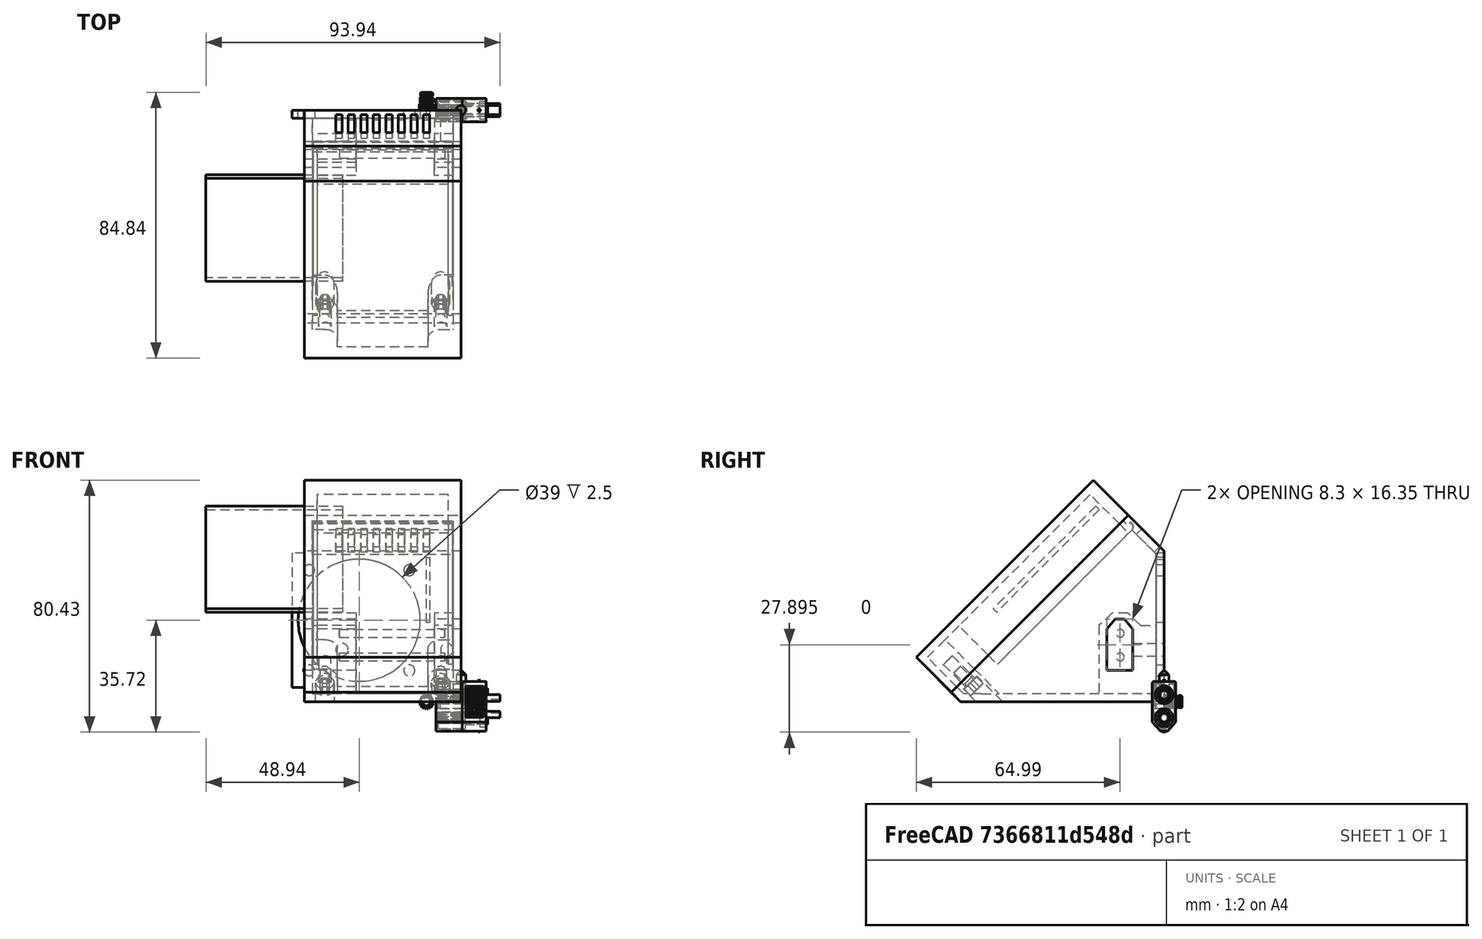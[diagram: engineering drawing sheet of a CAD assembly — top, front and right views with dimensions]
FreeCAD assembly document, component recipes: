
FREECAD ASSEMBLY — COMPONENT RECIPES ("moduleUSB_SimpleDual_001_SurBase35mm_012")

This assembly document has 12 components, labeled P0..P11 below (a component is one placed body or linked part). 5 of them carry a construction recipe — the FreeCAD feature program that regenerates the part from scratch, quoted from this document or its linked companion documents; the rest are supplied as boundary geometry only. No exploded tour is included for this assembly.
COMPONENT P0 — recipe-attached ("base", modeled in this document).
Construction recipe (the document's own serialized feature program — sketch geometry with constraints, then the solid features built on it; lengths are millimeters unless a unit is written):

FEATURE [PartDesign::FeatureBase] Clone
  BaseFeature = -> Slice_child0
FEATURE [PartDesign::Thickness] Thickness
  Base = -> Clone [Face7]
  BaseFeature = -> Clone
  Intersection = false
  Join = 0
  Mode = 0
  Reversed = true
  SupportTransform = false
  Value = 2.5
  expr: Value = <<sp>>.epaisseurParois
FEATURE [PartDesign::Plane] DatumPlane001  label="planXt"
  AttachmentOffset = pos=(0,0,-2.5) rot=(0,0,1;0rad)
  Length = 110.737
  MapMode = 5
  Placement = pos=(-2.5,6e-16,-6e-16) rot=(0.57735,0.57735,0.57735;2.0944rad)
  ResizeMode = 0
  Support = -> [YZ_Plane002]
  Width = 102.305
  expr: .AttachmentOffset.Base.z = -<<sp>>.epaisseurParois
FEATURE [Sketcher::SketchObject] Sketch002  label="sk_renfortXt"
  FullyConstrained = true
  MapMode = 5
  Placement = pos=(-2.5,6e-16,-6e-16) rot=(0.57735,0.57735,0.57735;2.0944rad)
  Support = -> [DatumPlane001]
  expr: .Constraints.dist = <<sp>>.xt60distanceAngleBord
  expr: .Constraints.epRf = <<sp>>.xt60epRenfort
  expr: Constraints[13] = <<sp>>.xt60largeurFetiere
  expr: Constraints[14] = <<sp>>.xt60hauteur
  expr: Constraints[15] = <<sp>>.xt60hauteurToit
  expr: Constraints[16] = <<sp>>.xt60base
  expr: Constraints[18] = .Constraints.dist
  expr: Constraints[31] = <<sp>>.epaisseurParois
  expr: Constraints[32] = .Constraints.epRf
  expr: Constraints[34] = .Constraints.epRf
  expr: Constraints[45] = <<sp>>.epaisseurParois
  sketch-geometry (17):
    g0: LineSegment StartX=-18.3 StartY=10 StartZ=0 EndX=-18.3 EndY=23.25 EndZ=0
    g1: LineSegment StartX=-18.3 StartY=23.25 StartZ=0 EndX=-15.65 EndY=25.75 EndZ=0
    g2: LineSegment StartX=-15.65 StartY=25.75 StartZ=0 EndX=-12.65 EndY=25.75 EndZ=0
    g3: LineSegment StartX=-12.65 StartY=25.75 StartZ=0 EndX=-10 EndY=23.25 EndZ=0
    g4: LineSegment StartX=-10 StartY=23.25 StartZ=0 EndX=-10 EndY=10 EndZ=0
    g5: LineSegment StartX=-10 StartY=10 StartZ=0 EndX=-18.3 EndY=10 EndZ=0
    g6: LineSegment StartX=-14.15 StartY=10 StartZ=0 EndX=-14.15 EndY=25.75 EndZ=0
    g7: LineSegment StartX=-16.6431 StartY=28.25 StartZ=0 EndX=-20.8 EndY=24.3284 EndZ=0
    g8: LineSegment StartX=-20.8 StartY=24.3284 StartZ=0 EndX=-20.8 EndY=2.5 EndZ=0
    g9: LineSegment StartX=-20.8 StartY=2.5 StartZ=0 EndX=-7.5 EndY=2.5 EndZ=0
    g10: LineSegment StartX=-7.5 StartY=2.5 StartZ=0 EndX=-7.5 EndY=24.3284 EndZ=0
    g11: LineSegment StartX=-7.5 StartY=24.3284 StartZ=0 EndX=-11.6569 EndY=28.25 EndZ=0
    g12: LineSegment StartX=-11.6569 StartY=28.25 StartZ=0 EndX=-16.6431 EndY=28.25 EndZ=0
    g13: LineSegment StartX=-7.5 StartY=24.3284 StartZ=0 EndX=-2.5 EndY=24.3284 EndZ=0
    g14: LineSegment StartX=-2.5 StartY=24.3284 StartZ=0 EndX=-2.5 EndY=2.5 EndZ=0
    g15: LineSegment StartX=-2.5 StartY=2.5 StartZ=0 EndX=-7.5 EndY=2.5 EndZ=0
    g16: LineSegment StartX=-7.5 StartY=2.5 StartZ=0 EndX=-7.5 EndY=24.3284 EndZ=0
  constraints (46):
    c: Vertical(g0)
    c: Coincident(g0,g1)
    c: Coincident(g1,g2)
    c: Horizontal(g2)
    c: Coincident(g2,g3)
    c: Coincident(g3,g4)
    c: Vertical(g4)
    c: Coincident(g4,g5)
    c: Coincident(g5,g0)
    c: Horizontal(g5)
    c: Symmetric(g1,g2,g6)
    c: Equal(g0,g4)
    c: Symmetric(g0,g4,g6)
    c: DistanceX(g2,g2) = 3
    c: DistanceY(g4,g4) = 13.25
    c: DistanceY(g3,g2) = 2.5
    c: DistanceX(g5,g5) = 8.3
    c: DistanceX(g4,g-1) = 10  'dist'
    c: DistanceY(g-1,g4) = 10
    c: Coincident(g7,g8)
    c: Vertical(g8)
    c: Coincident(g8,g9)
    c: Horizontal(g9)
    c: Coincident(g9,g10)
    c: Coincident(g10,g11)
    c: Coincident(g11,g12)
    c: Coincident(g12,g7)
    c: Symmetric(g7,g10,g6)
    c: Symmetric(g7,g11,g6)
    c: Symmetric(g8,g9,g6)
    c: DistanceX(g8,g0) = 2.5  'epRf'
    c: DistanceY(g-1,g9) = 2.5
    c: Distance(g7,g1) = 2.5
    c: Parallel(g1,g7)
    c: DistanceY(g2,g11) = 2.5
    c: Coincident(g13,g14)
    c: Coincident(g14,g15)
    c: Coincident(g15,g16)
    c: Coincident(g16,g13)
    c: Horizontal(g13)
    c: Horizontal(g15)
    c: Vertical(g14)
    c: Vertical(g16)
    c: Coincident(g13,g11)
    c: Horizontal(g14,g9)
    c: DistanceX(g14,g-1) = 2.5
FEATURE [PartDesign::Pad] Pad001  label="renfortXt"
  AllowMultiFace = false
  BaseFeature = -> Thickness
  Direction = (1,-1e-16,1e-16)
  Length = 45
  Length2 = 100
  Profile = -> Sketch002
  Reversed = true
  Type = 0
  expr: Length = <<sp>>.largeurModuleBase - 2 * <<sp>>.epaisseurParois
FEATURE [Sketcher::SketchObject] Sketch003  label="sk_trouXt"
  FullyConstrained = true
  MapMode = 5
  Placement = pos=(0,0,0) rot=(0.57735,0.57735,0.57735;2.0944rad)
  Support = -> [YZ_Plane002]
  expr: .Constraints.dist = <<sp>>.xt60distanceAngleBord
  expr: Constraints[13] = <<sp>>.xt60base
  expr: Constraints[14] = <<sp>>.xt60hauteur
  expr: Constraints[15] = <<sp>>.xt60hauteurToit + <<sp>>.xtJeu
  expr: Constraints[16] = <<sp>>.xt60largeurFetiere
  expr: Constraints[18] = .Constraints.dist
  sketch-geometry (7):
    g0: LineSegment StartX=-18.3 StartY=10 StartZ=0 EndX=-18.3 EndY=23.25 EndZ=0
    g1: LineSegment StartX=-18.3 StartY=23.25 StartZ=0 EndX=-15.65 EndY=26.35 EndZ=0
    g2: LineSegment StartX=-15.65 StartY=26.35 StartZ=0 EndX=-12.65 EndY=26.35 EndZ=0
    g3: LineSegment StartX=-12.65 StartY=26.35 StartZ=0 EndX=-10 EndY=23.25 EndZ=0
    g4: LineSegment StartX=-10 StartY=23.25 StartZ=0 EndX=-10 EndY=10 EndZ=0
    g5: LineSegment StartX=-10 StartY=10 StartZ=0 EndX=-18.3 EndY=10 EndZ=0
    g6: LineSegment StartX=-14.15 StartY=10 StartZ=0 EndX=-14.15 EndY=26.35 EndZ=0
  constraints (19):
    c: Vertical(g0)
    c: Coincident(g0,g1)
    c: Coincident(g1,g2)
    c: Horizontal(g2)
    c: Coincident(g2,g3)
    c: Coincident(g3,g4)
    c: Coincident(g4,g5)
    c: Coincident(g5,g0)
    c: Horizontal(g5)
    c: Symmetric(g1,g2,g6)
    c: Symmetric(g0,g3,g6)
    c: Vertical(g6)
    c: Symmetric(g0,g4,g6)
    c: DistanceX(g5,g5) = 8.3
    c: DistanceY(g4,g4) = 13.25
    c: DistanceY(g3,g2) = 3.1
    c: DistanceX(g2,g2) = 3
    c: DistanceX(g4,g-1) = 10  'dist'
    c: DistanceY(g-1,g4) = 10
FEATURE [PartDesign::Pocket] Pocket
  AllowMultiFace = false
  BaseFeature = -> Pad001
  Direction = (-1,2e-16,-3e-16)
  Length = 50
  Length2 = 100
  Profile = -> Sketch003
  Type = 0
  expr: Length = <<sp>>.largeurModuleBase
FEATURE [PartDesign::Plane] DatumPlane002  label="planDecoupeRenfortXt"
  AttachmentOffset = pos=(0,0,2.5) rot=(0,0,1;0rad)
  Length = 99.1505
  MapMode = 5
  Placement = pos=(0,-2.5,-6e-16) rot=(1,0,0;1.5708rad)
  ResizeMode = 0
  Support = -> [XZ_Plane002]
  Width = 101.269
  expr: .AttachmentOffset.Base.z = <<sp>>.epaisseurParois
FEATURE [Sketcher::SketchObject] Sketch004  label="sk_decoupRenfXt"
  FullyConstrained = true
  MapMode = 5
  Placement = pos=(0,-2.5,-6e-16) rot=(1,0,0;1.5708rad)
  Support = -> [DatumPlane002]
  expr: Constraints[10] = <<sp>>.xt60LongueurRenfortPetit + <<sp>>.epaisseurParois
  expr: Constraints[11] = <<sp>>.largeurModuleBase - (<<sp>>.xt60longueurRenfortGrand + <<sp>>.epaisseurParois)
  expr: Constraints[8] = <<sp>>.epaisseurParois
  expr: Constraints[9] = <<sp>>.xt60distanceAngleBord + <<sp>>.xt60hauteur + <<sp>>.xt60hauteurToit + <<sp>>.xt60epRenfort
  sketch-geometry (4):
    g0: LineSegment StartX=-33.5 StartY=28.25 StartZ=0 EndX=-8.5 EndY=28.25 EndZ=0
    g1: LineSegment StartX=-8.5 StartY=28.25 StartZ=0 EndX=-8.5 EndY=2.5 EndZ=0
    g2: LineSegment StartX=-8.5 StartY=2.5 StartZ=0 EndX=-33.5 EndY=2.5 EndZ=0
    g3: LineSegment StartX=-33.5 StartY=2.5 StartZ=0 EndX=-33.5 EndY=28.25 EndZ=0
  constraints (12):
    c: Coincident(g0,g1)
    c: Coincident(g1,g2)
    c: Coincident(g2,g3)
    c: Coincident(g3,g0)
    c: Horizontal(g0)
    c: Horizontal(g2)
    c: Vertical(g1)
    c: Vertical(g3)
    c: DistanceY(g-1,g1) = 2.5
    c: DistanceY(g-1,g0) = 28.25
    c: DistanceX(g1,g-1) = 8.5
    c: DistanceX(g2,g-1) = 33.5
FEATURE [PartDesign::Pocket] Pocket001  label="decoupeRenfXt"
  AllowMultiFace = false
  BaseFeature = -> Pocket
  Direction = (0,1,2e-16)
  Length = 23.3
  Length2 = 100
  Profile = -> Sketch004
  Reversed = true
  Type = 0
  expr: Length = <<sp>>.xt60distanceAngleBord + <<sp>>.xt60base + 2 * <<sp>>.xt60epRenfort
FEATURE [Sketcher::SketchObject] Sketch005  label="xt60PercagePostMale"
  FullyConstrained = true
  MapMode = 5
  Placement = pos=(0,0,0) rot=(1,0,0;1.5708rad)
  Support = -> [XZ_Plane002]
  expr: Constraints[0] = <<sp>>.insertDiamPercage
  expr: Constraints[1] = <<sp>>.insertDistanceTrouBordMale
  expr: Constraints[2] = <<sp>>.insertHauteur
  sketch-geometry (1):
    g0: Circle CenterX=-4.5 CenterY=16.625 CenterZ=0 NormalX=0 NormalY=0 NormalZ=1 AngleXU=0 Radius=2
  constraints (3):
    c: Diameter(g0) = 4
    c: DistanceX(g0,g-1) = 4.5
    c: DistanceY(g-1,g0) = 16.625
FEATURE [PartDesign::Pocket] Pocket002  label="insertXtMale"
  AllowMultiFace = false
  BaseFeature = -> Pocket001
  Direction = (0,1,2e-16)
  Length = 10
  Length2 = 100
  Profile = -> Sketch005
  Reversed = true
  Type = 0
  expr: Length = <<sp>>.insertProfondeurPercage
FEATURE [Sketcher::SketchObject] Sketch006  label="xt60PercagePostFem"
  FullyConstrained = true
  MapMode = 5
  Placement = pos=(0,0,0) rot=(1,0,0;1.5708rad)
  Support = -> [XZ_Plane002]
  expr: Constraints[0] = <<sp>>.insertDiamPercage
  expr: Constraints[1] = <<sp>>.insertDistanceTrouBordFem
  expr: Constraints[2] = <<sp>>.insertHauteur
  sketch-geometry (1):
    g0: Circle CenterX=-38 CenterY=16.625 CenterZ=0 NormalX=0 NormalY=0 NormalZ=1 AngleXU=0 Radius=2
  constraints (3):
    c: Diameter(g0) = 4
    c: DistanceX(g0,g-1) = 38
    c: DistanceY(g-1,g0) = 16.625
FEATURE [PartDesign::Pocket] Pocket003  label="insertXt60Fem"
  AllowMultiFace = false
  BaseFeature = -> Pocket002
  Direction = (0,1,2e-16)
  Length = 10
  Length2 = 100
  Profile = -> Sketch006
  Reversed = true
  Type = 0
  expr: Length = <<sp>>.insertProfondeurPercage
FEATURE [PartDesign::Plane] DatumPlane003
  AttachmentOffset = pos=(0,0,2.5) rot=(0,0,1;0rad)
  Length = 99.9633
  MapMode = 2
  Placement = pos=(0,0,2.5) rot=(0,0,1;0rad)
  ResizeMode = 0
  Support = -> [XY_Plane002]
  Width = 110.513
  expr: .AttachmentOffset.Base.z = <<sp>>.epaisseurParois
FEATURE [PartDesign::Plane] DatumPlane004  label="planTrancheur"
  AttachmentOffset = pos=(0,0,71) rot=(-1,0,0;0.785398rad)
  Length = 102.799
  MapMode = 5
  Placement = pos=(0,-71,-1.58e-14) rot=(1,0,0;0.785398rad)
  ResizeMode = 0
  Support = -> [XZ_Plane002]
  Width = 145.909
  expr: .AttachmentOffset.Base.z = <<sp>>.planTrancheur
FEATURE [Sketcher::SketchObject] Sketch008
  FullyConstrained = true
  MapMode = 5
  Placement = pos=(0,-71,-2.13e-14) rot=(1,0,0;0.785398rad)
  Support = -> [DatumPlane004]
  expr: .Constraints.dist = <<sp>>.epaisseurParois
  expr: Constraints[13] = <<sp>>.epaisseurParois
  expr: Constraints[16] = <<sp>>.insertDiamPercage / 2 + <<sp>>.insertFAVMargeDist
  expr: Constraints[1] = <<sp>>.insertFavDistAuZeroDuPLan
  expr: Constraints[21] = <<sp>>.insertFAVDistBord
  expr: Constraints[22] = <<sp>>.largeurModuleBase - <<sp>>.epaisseurParois
  sketch-geometry (7):
    g0: LineSegment StartX=-2.5 StartY=4.24264 StartZ=0 EndX=-47.5 EndY=4.24264 EndZ=0
    g1: LineSegment StartX=-6.5 StartY=14.7426 StartZ=0 EndX=-2.5 EndY=14.7426 EndZ=0
    g2: LineSegment StartX=-2.5 StartY=14.7426 StartZ=0 EndX=-2.5 EndY=6.74264 EndZ=0
    g3: LineSegment StartX=-2.5 StartY=6.74264 StartZ=0 EndX=-10.5 EndY=6.74264 EndZ=0
    g4: LineSegment StartX=-10.5 StartY=6.74264 StartZ=0 EndX=-10.5 EndY=10.7426 EndZ=0
    g5: ArcOfCircle CenterX=-6.5 CenterY=10.7426 CenterZ=0 NormalX=0 NormalY=0 NormalZ=1 AngleXU=0 Radius=4 StartAngle=1.5708 EndAngle=3.14159
    g6: LineSegment StartX=-6.5 StartY=10.7426 StartZ=0 EndX=-6.5 EndY=6.74264 EndZ=0
  constraints (23):
    c: Horizontal(g0)
    c: DistanceY(g-1,g0) = 4.24264
    c: DistanceX(g0,g-1) = 2.5  'dist'
    c: Horizontal(g1)
    c: Coincident(g1,g2)
    c: Vertical(g2)
    c: Coincident(g2,g3)
    c: Horizontal(g3)
    c: Coincident(g3,g4)
    c: Vertical(g4)
    c: Vertical(g2,g0)
    c: Equal(g3,g2)
    c: Equal(g4,g1)
    c: DistanceY(g0,g2) = 2.5
    c: Coincident(g5,g4)
    c: Coincident(g5,g1)
    c: DistanceX(g5,g2) = 4
    c: Coincident(g6,g5)
    c: PointOnObject(g6,g3)
    c: Vertical(g6)
    c: Vertical(g5,g1)
    c: DistanceX(g3,g3) = 8
    c: DistanceX(g0,g-1) = 47.5
FEATURE [PartDesign::Pad] Pad003  label="padTrouFAVDroite"
  AllowMultiFace = false
  BaseFeature = -> Pocket003
  Direction = (0,-0.707107,0.707107)
  Length = 10
  Length2 = 100
  Profile = -> Sketch008
  Reversed = true
  Type = 3
  UpToFace = -> DatumPlane003
FEATURE [Sketcher::SketchObject] Sketch009
  FullyConstrained = true
  MapMode = 5
  Placement = pos=(0,-71,-2.13e-14) rot=(1,0,0;0.785398rad)
  Support = -> [DatumPlane004]
  expr: .Constraints.larg = <<sp>>.insertFAVDistBord
  expr: Constraints[11] = .Constraints.larg / 2
  expr: Constraints[12] = <<sp>>.largeurModuleBase
  expr: Constraints[13] = <<sp>>.insertFavDistAuZeroDuPLan
  expr: Constraints[14] = <<sp>>.epaisseurParois
  expr: Constraints[15] = <<sp>>.epaisseurParois
  expr: Constraints[8] = .Constraints.larg
  sketch-geometry (6):
    g0: LineSegment StartX=-47.5 StartY=6.74264 StartZ=0 EndX=-39.5 EndY=6.74264 EndZ=0
    g1: LineSegment StartX=-39.5 StartY=6.74264 StartZ=0 EndX=-39.5 EndY=10.7426 EndZ=0
    g2: LineSegment StartX=-43.5 StartY=14.7426 StartZ=0 EndX=-47.5 EndY=14.7426 EndZ=0
    g3: LineSegment StartX=-47.5 StartY=14.7426 StartZ=0 EndX=-47.5 EndY=6.74264 EndZ=0
    g4: ArcOfCircle CenterX=-43.5 CenterY=10.7426 CenterZ=0 NormalX=0 NormalY=0 NormalZ=1 AngleXU=0 Radius=4 StartAngle=0 EndAngle=1.5708
    g5: GeomPoint X=-50 Y=4.24264 Z=0
  constraints (16):
    c: Coincident(g0,g1)
    c: Coincident(g2,g3)
    c: Coincident(g3,g0)
    c: Horizontal(g0)
    c: Horizontal(g2)
    c: Vertical(g1)
    c: Vertical(g3)
    c: DistanceX(g0,g0) = 8  'larg'
    c: DistanceY(g3,g3) = 8
    c: Tangent(g2,g4) = -1.5708
    c: Tangent(g1,g4) = -1.5708
    c: DistanceX(g0,g4) = 4
    c: DistanceX(g5,g-1) = 50
    c: DistanceY(g-1,g5) = 4.24264
    c: DistanceX(g5,g0) = 2.5
    c: DistanceY(g5,g0) = 2.5
FEATURE [PartDesign::Pad] Pad004  label="padTrouFavGauche"
  AllowMultiFace = false
  BaseFeature = -> Pad003
  Direction = (0,-0.707107,0.707107)
  Length = 10
  Length2 = 100
  Profile = -> Sketch009
  Type = 3
  UpToFace = -> DatumPlane003 [Plane]
FEATURE [Sketcher::SketchObject] Sketch010
  FullyConstrained = true
  MapMode = 5
  Placement = pos=(0,-71,-2.13e-14) rot=(1,0,0;0.785398rad)
  Support = -> [DatumPlane004]
  expr: Constraints[0] = <<sp>>.insertFAVDistBord / 2 + <<sp>>.epaisseurParois
  expr: Constraints[1] = <<sp>>.insertFavDistAuZeroDuPLan + <<sp>>.epaisseurParois + <<sp>>.insertFAVDistBord / 2
  expr: Constraints[2] = <<sp>>.insertDiamPercage
  sketch-geometry (1):
    g0: Circle CenterX=-6.5 CenterY=10.7426 CenterZ=0 NormalX=0 NormalY=0 NormalZ=1 AngleXU=0 Radius=2
  constraints (3):
    c: DistanceX(g0,g-1) = 6.5
    c: DistanceY(g-1,g0) = 10.7426
    c: Diameter(g0) = 4
FEATURE [PartDesign::Pocket] Pocket004  label="trouDroit"
  AllowMultiFace = false
  BaseFeature = -> Pad004
  Direction = (0,0.707107,-0.707107)
  Length = 5
  Length2 = 100
  Profile = -> Sketch010
  Type = 1
FEATURE [Sketcher::SketchObject] Sketch011
  FullyConstrained = true
  MapMode = 5
  Placement = pos=(0,-71,-2.13e-14) rot=(1,0,0;0.785398rad)
  Support = -> [DatumPlane004]
  expr: Constraints[0] = <<sp>>.insertDiamPercage
  expr: Constraints[1] = <<sp>>.largeurModuleBase - <<sp>>.epaisseurParois - <<sp>>.insertFAVDistBord / 2
  expr: Constraints[2] = <<sp>>.insertFavDistAuZeroDuPLan + <<sp>>.epaisseurParois + <<sp>>.insertFAVDistBord / 2
  sketch-geometry (1):
    g0: Circle CenterX=-43.5 CenterY=10.7426 CenterZ=0 NormalX=0 NormalY=0 NormalZ=1 AngleXU=0 Radius=2
  constraints (3):
    c: Diameter(g0) = 4
    c: DistanceX(g0,g-1) = 43.5
    c: DistanceY(g-1,g0) = 10.7426
FEATURE [PartDesign::Pocket] Pocket005  label="trouGauche"
  AllowMultiFace = false
  BaseFeature = -> Pocket004
  Direction = (0,0.707107,-0.707107)
  Length = 5
  Length2 = 100
  Profile = -> Sketch011
  Type = 1
FEATURE [PartDesign::Plane] DatumPlane005  label="planTeteVisFav"
  AttachmentOffset = pos=(0,0,68) rot=(-1,0,0;0.785398rad)
  Length = 102.799
  MapMode = 5
  Placement = pos=(0,-68,-1.51e-14) rot=(1,0,0;0.785398rad)
  ResizeMode = 0
  Support = -> [XZ_Plane002]
  Width = 145.909
  expr: .AttachmentOffset.Base.z = <<sp>>.planTrancheur - 3
FEATURE [Sketcher::SketchObject] Sketch012
  ExternalGeometry = -> [Pocket005]
  FullyConstrained = true
  MapMode = 5
  Placement = pos=(0,-68,-1.42e-14) rot=(1,0,0;0.785398rad)
  Support = -> [DatumPlane005]
  expr: Constraints[1] = <<sp>>.visM3DiamEncastrement
  sketch-geometry (2):
    g0: Circle CenterX=-6.5 CenterY=8.62132 CenterZ=0 NormalX=0 NormalY=0 NormalZ=1 AngleXU=0 Radius=3
    g1: Circle CenterX=-43.5 CenterY=8.62132 CenterZ=0 NormalX=0 NormalY=0 NormalZ=1 AngleXU=0 Radius=3
  constraints (4):
    c: Equal(g0,g1)
    c: Diameter(g1) = 6
    c: Coincident(g1,g-4)
    c: Coincident(g-3,g0)
FEATURE [PartDesign::Pocket] Pocket006  label="evidementTeteVisFav"
  AllowMultiFace = false
  BaseFeature = -> Pocket005
  Direction = (0,0.707107,-0.707107)
  Length = 20
  Length2 = 100
  Profile = -> Sketch012
  Type = 1
FEATURE [Sketcher::SketchObject] Sketch014
  FullyConstrained = true
  MapMode = 5
  Placement = pos=(0,0,0) rot=(1,0,0;1.5708rad)
  Support = -> [XZ_Plane002]
  expr: Constraints[12] = <<sp>>.xt60distanceAngleBord + <<sp>>.xt60hauteur + <<sp>>.ventilDistBordFente
  expr: Constraints[13] = <<sp>>.ventilLargeurFentes
  expr: Constraints[14] = <<sp>>.ventilEcartfente / 2
  expr: Constraints[15] = <<sp>>.hauteurDuDos - <<sp>>.ventilDistBordFente
  expr: Constraints[2] = <<sp>>.hauteurDuDos
  expr: Constraints[3] = <<sp>>.largeurModuleBase / 2
  sketch-geometry (5):
    g0: LineSegment StartX=-25 StartY=0 StartZ=0 EndX=-25 EndY=48.1371 EndZ=0
    g1: LineSegment StartX=-28 StartY=46.1371 StartZ=0 EndX=-26 EndY=46.1371 EndZ=0
    g2: LineSegment StartX=-26 StartY=46.1371 StartZ=0 EndX=-26 EndY=25.25 EndZ=0
    g3: LineSegment StartX=-26 StartY=25.25 StartZ=0 EndX=-28 EndY=25.25 EndZ=0
    g4: LineSegment StartX=-28 StartY=25.25 StartZ=0 EndX=-28 EndY=46.1371 EndZ=0
  constraints (16):
    c: PointOnObject(g0,g-1)
    c: Vertical(g0)
    c: DistanceY(g0,g0) = 48.1371
    c: DistanceX(g0,g-1) = 25
    c: Coincident(g1,g2)
    c: Coincident(g2,g3)
    c: Coincident(g3,g4)
    c: Coincident(g4,g1)
    c: Horizontal(g1)
    c: Horizontal(g3)
    c: Vertical(g2)
    c: Vertical(g4)
    c: DistanceY(g-1,g2) = 25.25
    c: DistanceX(g1,g1) = 2
    c: DistanceX(g2,g0) = 1
    c: DistanceY(g-1,g1) = 46.1371
FEATURE [PartDesign::Pocket] Pocket008  label="ventilFente1"
  AllowMultiFace = false
  BaseFeature = -> Pocket006
  Direction = (0,1,2e-16)
  Length = 2.5
  Length2 = 100
  Profile = -> Sketch014
  Reversed = true
  Type = 0
  expr: Length = <<sp>>.epaisseurParois
FEATURE [PartDesign::LinearPattern] LinearPattern  label="ventilDosRepeat1"
  BaseFeature = -> Pocket008
  Direction = -> Sketch014 [H_Axis]
  Length = 12
  Occurrences = 4
  Originals = -> [Pocket008]
  Reversed = true
  expr: Length = <<sp>>.ventilLargeurRepet
  expr: Occurrences = <<sp>>.ventilNbrFents
FEATURE [PartDesign::LinearPattern] LinearPattern001  label="ventilDosRepeat2"
  BaseFeature = -> LinearPattern
  Direction = -> Sketch014 [H_Axis]
  Length = 16
  Occurrences = 5
  Originals = -> [Pocket008]
  expr: Length = <<sp>>.ventilLargeurRepet + <<sp>>.ventilEcartfente + <<sp>>.ventilLargeurFentes
  expr: Occurrences = <<sp>>.ventilNbrFents + 1
FEATURE [PartDesign::Plane] DatumPlane006  label="planVentilSup"
  AttachmentOffset = pos=(0,0,-48.1371) rot=(1,0,0;0.785398rad)
  Length = 102.799
  MapMode = 5
  Placement = pos=(0,48.1371,1.07e-14) rot=(1,0,0;2.35619rad)
  ResizeMode = 0
  Support = -> [XZ_Plane002]
  Width = 145.909
  expr: .AttachmentOffset.Base.z = -<<sp>>.hauteurDuDos
FEATURE [Sketcher::SketchObject] Sketch015
  FullyConstrained = true
  MapMode = 5
  Placement = pos=(0,48.1371,1.07e-14) rot=(1,0,0;2.35619rad)
  Support = -> [DatumPlane006]
  expr: Constraints[10] = <<sp>>.ventilLargeurFentes
  expr: Constraints[11] = (<<sp>>.largeurModuleBase + <<sp>>.ventilEcartfente) / 2
  expr: Constraints[8] = <<sp>>.distanceAuZeroPlanBorArriere + <<sp>>.ventilDistBordFente
  expr: Constraints[9] = <<sp>>.longPetitRetSupSansFav - 2 * <<sp>>.ventilDistBordFente - <<sp>>.favBordureProf
  sketch-geometry (4):
    g0: LineSegment StartX=-26 StartY=78.0926 StartZ=0 EndX=-28 EndY=78.0926 EndZ=0
    g1: LineSegment StartX=-28 StartY=78.0926 StartZ=0 EndX=-28 EndY=70.0761 EndZ=0
    g2: LineSegment StartX=-28 StartY=70.0761 StartZ=0 EndX=-26 EndY=70.0761 EndZ=0
    g3: LineSegment StartX=-26 StartY=70.0761 StartZ=0 EndX=-26 EndY=78.0926 EndZ=0
  constraints (12):
    c: Coincident(g0,g1)
    c: Coincident(g1,g2)
    c: Coincident(g2,g3)
    c: Coincident(g3,g0)
    c: Horizontal(g0)
    c: Horizontal(g2)
    c: Vertical(g1)
    c: Vertical(g3)
    c: DistanceY(g-1,g2) = 70.0761
    c: DistanceY(g2,g0) = 8.01652
    c: DistanceX(g0,g0) = 2
    c: DistanceX(g2,g-1) = 26
FEATURE [PartDesign::Pocket] Pocket009  label="ventilSupFente"
  AllowMultiFace = false
  BaseFeature = -> LinearPattern001
  Direction = (0,0.707107,0.707107)
  Length = 5
  Length2 = 100
  Profile = -> Sketch015
  Reversed = true
  Type = 0
FEATURE [PartDesign::LinearPattern] LinearPattern002  label="ventilSupRepeat1"
  BaseFeature = -> Pocket009
  Direction = -> Sketch015 [H_Axis]
  Length = 12
  Occurrences = 4
  Originals = -> [Pocket009]
  Reversed = true
  expr: Length = <<sp>>.ventilLargeurRepet
  expr: Occurrences = <<sp>>.ventilNbrFents
FEATURE [PartDesign::LinearPattern] LinearPattern003  label="ventilSupRepeat2"
  BaseFeature = -> LinearPattern002
  Direction = -> Sketch015 [H_Axis]
  Length = 16
  Occurrences = 5
  Originals = -> [Pocket009]
  expr: Length = <<sp>>.ventilLargeurRepet + <<sp>>.ventilEcartfente + <<sp>>.ventilLargeurFentes
  expr: Occurrences = <<sp>>.ventilNbrFents + 1
FEATURE [PartDesign::Body] Body001  label="base"
  BaseFeature = -> Slice_child0
  Group = -> [Clone,Thickness,DatumPlane001,Sketch002,Pad001,Sketch003,Pocket,DatumPlane002,Sketch004,Pocket001,Sketch005,Pocket002,Sketch006,Pocket003,DatumPlane003,DatumPlane004,Sketch008,Pad003,Sketch009,Pad004,Sketch010,Pocket004,Sketch011,Pocket005,DatumPlane005,Sketch012,Pocket006,Sketch014,Pocket008,LinearPattern,LinearPattern001,DatumPlane006,Sketch015,Pocket009,LinearPattern002,LinearPattern003,+9 more]
  Origin = -> Origin002
  Tip = -> Pocket019
COMPONENT P1 — recipe-attached ("faceAvant", modeled in this document).
Construction recipe (the document's own serialized feature program — sketch geometry with constraints, then the solid features built on it; lengths are millimeters unless a unit is written):

FEATURE [PartDesign::FeatureBase] Clone001
  BaseFeature = -> Slice_child1
FEATURE [PartDesign::Thickness] Thickness001
  Base = -> Clone001 [Face5]
  BaseFeature = -> Clone001
  Intersection = false
  Join = 0
  Mode = 0
  Reversed = true
  SupportTransform = false
  Value = 2.5
  expr: Value = <<sp>>.epaisseurParois
FEATURE [PartDesign::Plane] DatumPlane007  label="planTrancheurBis"
  AttachmentOffset = pos=(0,0,71) rot=(-1,0,0;0.785398rad)
  Length = 95.5901
  MapMode = 5
  Placement = pos=(0,-71,-1.58e-14) rot=(1,0,0;0.785398rad)
  ResizeMode = 0
  Support = -> [XZ_Plane003]
  Width = 161.907
  expr: .AttachmentOffset.Base.z = <<sp>>.planTrancheur
FEATURE [Sketcher::SketchObject] Sketch016  label="sk_insertFavDroit"
  FullyConstrained = true
  MapMode = 5
  Placement = pos=(0,-71,-2.13e-14) rot=(1,0,0;0.785398rad)
  Support = -> [DatumPlane007]
  expr: Constraints[11] = <<sp>>.insertFAVDistBord
  expr: Constraints[14] = <<sp>>.insertFAVDistBord / 2
  expr: Constraints[7] = <<sp>>.epaisseurParois
  expr: Constraints[8] = <<sp>>.insertFavDistAuZeroDuPLan + <<sp>>.epaisseurParois
  expr: Constraints[9] = <<sp>>.insertFAVDistBord
  sketch-geometry (5):
    g0: LineSegment StartX=-6.5 StartY=14.7426 StartZ=0 EndX=-2.5 EndY=14.7426 EndZ=0
    g1: LineSegment StartX=-2.5 StartY=14.7426 StartZ=0 EndX=-2.5 EndY=6.74264 EndZ=0
    g2: LineSegment StartX=-2.5 StartY=6.74264 StartZ=0 EndX=-10.5 EndY=6.74264 EndZ=0
    g3: LineSegment StartX=-10.5 StartY=6.74264 StartZ=0 EndX=-10.5 EndY=10.7426 EndZ=0
    g4: ArcOfCircle CenterX=-6.5 CenterY=10.7426 CenterZ=0 NormalX=0 NormalY=0 NormalZ=1 AngleXU=0 Radius=4 StartAngle=1.5708 EndAngle=3.14159
  constraints (15):
    c: Horizontal(g0)
    c: Coincident(g0,g1)
    c: Vertical(g1)
    c: Coincident(g1,g2)
    c: Horizontal(g2)
    c: Coincident(g2,g3)
    c: Vertical(g3)
    c: DistanceX(g1,g-1) = 2.5
    c: DistanceY(g-1,g1) = 6.74264
    c: DistanceY(g1,g1) = 8
    c: Equal(g3,g0)
    c: DistanceX(g2,g2) = 8
    c: Coincident(g4,g0)
    c: Tangent(g4,g3) = 1.5708
    c: DistanceX(g4,g1) = 4
FEATURE [PartDesign::Pad] Pad005  label="padInsertFavDroit"
  AllowMultiFace = false
  BaseFeature = -> Thickness001
  Direction = (0,-0.707107,0.707107)
  Length = 10
  Length2 = 100
  Profile = -> Sketch016
  Type = 2
FEATURE [Sketcher::SketchObject] Sketch017  label="sp_padInserFavGauch"
  FullyConstrained = true
  MapMode = 5
  Placement = pos=(0,-71,-2.13e-14) rot=(1,0,0;0.785398rad)
  Support = -> [DatumPlane007]
  expr: Constraints[10] = <<sp>>.insertFAVDistBord
  expr: Constraints[12] = <<sp>>.insertFAVDistBord / 2
  expr: Constraints[13] = <<sp>>.largeurModuleBase
  expr: Constraints[14] = <<sp>>.insertFavDistAuZeroDuPLan
  expr: Constraints[15] = <<sp>>.epaisseurParois
  expr: Constraints[16] = <<sp>>.epaisseurParois
  sketch-geometry (6):
    g0: LineSegment StartX=-43.5 StartY=14.7426 StartZ=0 EndX=-47.5 EndY=14.7426 EndZ=0
    g1: LineSegment StartX=-47.5 StartY=14.7426 StartZ=0 EndX=-47.5 EndY=6.74264 EndZ=0
    g2: LineSegment StartX=-47.5 StartY=6.74264 StartZ=0 EndX=-39.5 EndY=6.74264 EndZ=0
    g3: LineSegment StartX=-39.5 StartY=6.74264 StartZ=0 EndX=-39.5 EndY=10.7426 EndZ=0
    g4: ArcOfCircle CenterX=-43.5 CenterY=10.7426 CenterZ=0 NormalX=0 NormalY=0 NormalZ=1 AngleXU=0 Radius=4 StartAngle=6.0202e-12 EndAngle=1.5708
    g5: GeomPoint X=-50 Y=4.24264 Z=0
  constraints (17):
    c: Horizontal(g0)
    c: Coincident(g0,g1)
    c: Vertical(g1)
    c: Coincident(g1,g2)
    c: Horizontal(g2)
    c: Coincident(g2,g3)
    c: Vertical(g3)
    c: Equal(g3,g0)
    c: Equal(g2,g1)
    c: Coincident(g0,g4)
    c: DistanceX(g2,g2) = 8
    c: Tangent(g4,g3) = -1.5708
    c: DistanceX(g0,g0) = 4
    c: DistanceX(g5,g-1) = 50
    c: DistanceY(g-1,g5) = 4.24264
    c: DistanceY(g5,g1) = 2.5
    c: DistanceX(g5,g1) = 2.5
FEATURE [PartDesign::Pad] Pad006  label="padInsertFavGauch"
  AllowMultiFace = false
  BaseFeature = -> Pad005
  Direction = (0,-0.707107,0.707107)
  Length = 10
  Length2 = 100
  Profile = -> Sketch017
  Type = 2
FEATURE [Sketcher::SketchObject] Sketch018  label="skPercageInsertFavDroit"
  FullyConstrained = true
  MapMode = 5
  Placement = pos=(0,-71,-2.13e-14) rot=(1,0,0;0.785398rad)
  Support = -> [DatumPlane007]
  expr: Constraints[0] = <<sp>>.insertDiamPercage
  expr: Constraints[1] = <<sp>>.insertFavDistAuZeroDuPLan + <<sp>>.epaisseurParois + <<sp>>.insertFAVDistBord / 2
  expr: Constraints[2] = <<sp>>.epaisseurParois + <<sp>>.insertFAVDistBord / 2
  expr: Constraints[7] = <<sp>>.largeurModuleBase - 2 * <<sp>>.epaisseurParois - <<sp>>.insertFAVDistBord
  sketch-geometry (3):
    g0: Circle CenterX=-6.5 CenterY=10.7426 CenterZ=0 NormalX=0 NormalY=0 NormalZ=1 AngleXU=0 Radius=2
    g1: Circle CenterX=-43.5 CenterY=10.7426 CenterZ=0 NormalX=0 NormalY=0 NormalZ=1 AngleXU=0 Radius=2
    g2: LineSegment StartX=-43.5 StartY=10.7426 StartZ=0 EndX=-6.5 EndY=10.7426 EndZ=0
  constraints (8):
    c: Diameter(g0) = 4
    c: DistanceY(g-1,g0) = 10.7426
    c: DistanceX(g0,g-1) = 6.5
    c: Equal(g0,g1)
    c: Coincident(g2,g1)
    c: Coincident(g2,g0)
    c: Horizontal(g2)
    c: DistanceX(g2,g2) = 37
FEATURE [PartDesign::Pocket] Pocket010  label="trouInsertFavDroit"
  AllowMultiFace = false
  BaseFeature = -> Pad006
  Direction = (0,0.707107,-0.707107)
  Length = 8
  Length2 = 100
  Profile = -> Sketch018
  Reversed = true
  Type = 0
  expr: Length = <<sp>>.insertFavProfondeur
FEATURE [PartDesign::Plane] DatumPlane011  label="planFaceAvant"
  AttachmentOffset = pos=(0,0,93.2843) rot=(-1,0,0;0.785398rad)
  Length = 95.5901
  MapMode = 5
  Placement = pos=(0,-93.2843,-2.07e-14) rot=(1,0,0;0.785398rad)
  ResizeMode = 0
  Support = -> [XZ_Plane003]
  Width = 161.907
  expr: .AttachmentOffset.Base.z = <<sp>>.planFaceAvant
FEATURE [Sketcher::SketchObject] Sketch030  label="sk_rebordFav"
  FullyConstrained = true
  MapMode = 5
  Placement = pos=(0,-71,-2.13e-14) rot=(1,0,0;0.785398rad)
  Support = -> [DatumPlane007]
  expr: Constraints[0] = <<sp>>.insertFavDistAuZeroDuPLan
  expr: Constraints[19] = <<sp>>.epaisseurParois
  expr: Constraints[20] = <<sp>>.favEpBordure
  expr: Constraints[21] = <<sp>>.favDistBordPlan
  expr: Constraints[22] = <<sp>>.largeurModuleBase - 2 * <<sp>>.epaisseurParois
  expr: Constraints[23] = <<sp>>.favEpBordure
  expr: Constraints[24] = <<sp>>.Face - <<sp>>.epaisseurParois
  expr: Constraints[25] = <<sp>>.favEpBordure
  sketch-geometry (9):
    g0: GeomPoint X=0 Y=4.24264 Z=0
    g1: LineSegment StartX=-47.5 StartY=20.9853 StartZ=0 EndX=-47.5 EndY=81.7426 EndZ=0
    g2: LineSegment StartX=-47.5 StartY=81.7426 StartZ=0 EndX=-2.5 EndY=81.7426 EndZ=0
    g3: LineSegment StartX=-2.5 StartY=81.7426 StartZ=0 EndX=-2.5 EndY=20.9853 EndZ=0
    g4: LineSegment StartX=-2.5 StartY=20.9853 StartZ=0 EndX=-4 EndY=20.9853 EndZ=0
    g5: LineSegment StartX=-4 StartY=20.9853 StartZ=0 EndX=-4 EndY=80.2426 EndZ=0
    g6: LineSegment StartX=-4 StartY=80.2426 StartZ=0 EndX=-46 EndY=80.2426 EndZ=0
    g7: LineSegment StartX=-46 StartY=80.2426 StartZ=0 EndX=-46 EndY=20.9853 EndZ=0
    g8: LineSegment StartX=-46 StartY=20.9853 StartZ=0 EndX=-47.5 EndY=20.9853 EndZ=0
  constraints (26):
    c: DistanceY(g-1,g0) = 4.24264
    c: Vertical(g0,g-1)
    c: Vertical(g1)
    c: Coincident(g1,g2)
    c: Horizontal(g2)
    c: Coincident(g2,g3)
    c: Vertical(g3)
    c: Coincident(g3,g4)
    c: Horizontal(g4)
    c: Coincident(g4,g5)
    c: Vertical(g5)
    c: Coincident(g5,g6)
    c: Horizontal(g6)
    c: Coincident(g6,g7)
    c: Vertical(g7)
    c: Coincident(g7,g8)
    c: Coincident(g8,g1)
    c: Horizontal(g8)
    c: Horizontal(g7,g4)
    c: DistanceX(g3,g0) = 2.5
    c: DistanceX(g4,g4) = 1.5
    c: DistanceY(g0,g3) = 16.7426
    c: DistanceX(g1,g3) = 45
    c: DistanceY(g5,g2) = 1.5
    c: DistanceY(g0,g2) = 77.5
    c: DistanceX(g1,g7) = 1.5
FEATURE [PartDesign::Pad] Pad014  label="favRebordSupport"
  AllowMultiFace = false
  BaseFeature = -> Pocket010
  Direction = (0,-0.707107,0.707107)
  Length = 10
  Length2 = 100
  Profile = -> Sketch030
  Type = 3
  UpToFace = -> Pocket010 [Face13]
FEATURE [PartDesign::Pad] Pad015  label="favRebord"
  AllowMultiFace = false
  BaseFeature = -> Pad014
  Direction = (0,-0.707107,0.707107)
  Length = 4.15
  Length2 = 100
  Profile = -> Sketch030
  Reversed = true
  Type = 0
  expr: Length = <<sp>>.favBordureProf
FEATURE [Sketcher::SketchObject] Sketch031  label="sk_bourlet"
  ExternalGeometry = -> [Pad015]
  FullyConstrained = true
  MapMode = 5
  Placement = pos=(-2.5,0,0) rot=(0.57735,0.57735,0.57735;2.0944rad)
  Support = -> [Pad015]
  expr: Constraints[3] = <<sp>>.bourletMaintientRayon - <<sp>>.bourletRayonJeu
  sketch-geometry (2):
    g0: ArcOfCircle CenterX=-11.184 CenterY=55.7855 CenterZ=0 NormalX=0 NormalY=0 NormalZ=1 AngleXU=0 Radius=1.3 StartAngle=5.49779 EndAngle=8.63938
    g1: LineSegment StartX=-12.1032 StartY=56.7048 StartZ=0 EndX=-10.2647 EndY=54.8663 EndZ=0
  constraints (6):
    c: Coincident(g0,g-3)
    c: PointOnObject(g0,g-3)
    c: PointOnObject(g0,g-3)
    c: Radius(g0) = 1.3
    c: Coincident(g1,g0)
    c: Coincident(g1,g0)
FEATURE [PartDesign::Pad] Pad016  label="bourlet"
  AllowMultiFace = false
  BaseFeature = -> Pad015
  Direction = (1,0,0)
  Length = 10
  Length2 = 100
  Profile = -> Sketch031
  Reversed = true
  Type = 3
  UpToFace = -> Pad015 [Face11]
FEATURE [Sketcher::SketchObject] Sketch039
  FullyConstrained = true
  MapMode = 5
  Placement = pos=(0,-71,-2.13e-14) rot=(1,0,0;0.785398rad)
  Support = -> [DatumPlane007]
  expr: Constraints[20] = <<sp>>.favBordureJeu / 2
  expr: Constraints[21] = <<sp>>.epaisseurParois
  expr: Constraints[22] = <<sp>>.largeurModuleBase - 2 * <<sp>>.epaisseurParois
  expr: Constraints[23] = <<sp>>.insertFavDistAuZeroDuPLan + <<sp>>.favDistBordPlan
  expr: Constraints[27] = <<sp>>.insertFavDistAuZeroDuPLan + <<sp>>.Face - <<sp>>.epaisseurParois + <<sp>>.bourletMaintientRayon
  sketch-geometry (10):
    g0: LineSegment StartX=-47.5 StartY=83.2426 StartZ=0 EndX=-47.25 EndY=83.2426 EndZ=0
    g1: LineSegment StartX=-47.25 StartY=83.2426 StartZ=0 EndX=-47.25 EndY=20.9853 EndZ=0
    g2: LineSegment StartX=-47.25 StartY=20.9853 StartZ=0 EndX=-47.5 EndY=20.9853 EndZ=0
    g3: LineSegment StartX=-47.5 StartY=20.9853 StartZ=0 EndX=-47.5 EndY=83.2426 EndZ=0
    g4: LineSegment StartX=-2.5 StartY=83.2426 StartZ=0 EndX=-2.75 EndY=83.2426 EndZ=0
    g5: LineSegment StartX=-2.75 StartY=83.2426 StartZ=0 EndX=-2.75 EndY=20.9853 EndZ=0
    g6: LineSegment StartX=-2.75 StartY=20.9853 StartZ=0 EndX=-2.5 EndY=20.9853 EndZ=0
    g7: LineSegment StartX=-2.5 StartY=20.9853 StartZ=0 EndX=-2.5 EndY=83.2426 EndZ=0
    g8: LineSegment StartX=-47.25 StartY=20.9853 StartZ=0 EndX=-2.5 EndY=20.9853 EndZ=0
    g9: LineSegment StartX=-2.75 StartY=83.2426 StartZ=0 EndX=-47.25 EndY=83.2426 EndZ=0
  constraints (28):
    c: Coincident(g0,g1)
    c: Coincident(g1,g2)
    c: Coincident(g2,g3)
    c: Coincident(g3,g0)
    c: Horizontal(g0)
    c: Horizontal(g2)
    c: Vertical(g1)
    c: Vertical(g3)
    c: Coincident(g4,g5)
    c: Coincident(g5,g6)
    c: Coincident(g6,g7)
    c: Coincident(g7,g4)
    c: Horizontal(g4)
    c: Horizontal(g6)
    c: Vertical(g5)
    c: Vertical(g7)
    c: Coincident(g8,g1)
    c: Coincident(g8,g6)
    c: Horizontal(g8)
    c: Equal(g2,g6)
    c: DistanceX(g2,g2) = 0.25
    c: DistanceX(g6,g-1) = 2.5
    c: DistanceX(g2,g6) = 45
    c: DistanceY(g-1,g6) = 20.9853
    c: Coincident(g9,g4)
    c: Coincident(g9,g0)
    c: Horizontal(g9)
    c: DistanceY(g-1,g4) = 83.2426
FEATURE [PartDesign::Pocket] Pocket018  label="ajoutJeuLevreFav"
  BaseFeature = -> Pad016
  Direction = (0,0.707107,-0.707107)
  Length = 4.15
  Length2 = 5
  Profile = -> Sketch039
  ReferenceAxis = -> Sketch039 [N_Axis]
  Type = 0
  expr: Length = <<sp>>.favBordureProf
FEATURE [PartDesign::Plane] DatumPlane016  label="planFaceAvantPCB"
  AttachmentOffset = pos=(0,0,84.28) rot=(-1,0,0;0.785398rad)
  Length = 95.5901
  MapMode = 5
  Placement = pos=(0,-84.28,-1.87e-14) rot=(1,0,0;0.785398rad)
  ResizeMode = 0
  Support = -> [XZ_Plane003]
  Width = 161.907
FEATURE [Sketcher::SketchObject] Sketch044  label="pcbFavSk"
  FullyConstrained = false
  MapMode = 5
  Placement = pos=(0,-84.28,-1.42e-14) rot=(1,0,0;0.785398rad)
  Support = -> [DatumPlane016]
  sketch-geometry (4):
    g0: LineSegment StartX=-80.4521 StartY=87.0314 StartZ=0 EndX=-37.8912 EndY=87.0314 EndZ=0
    g1: LineSegment StartX=-37.8912 StartY=87.0314 StartZ=0 EndX=-37.8912 EndY=42.7351 EndZ=0
    g2: LineSegment StartX=-37.8912 StartY=42.7351 StartZ=0 EndX=-80.4521 EndY=42.7351 EndZ=0
    g3: LineSegment StartX=-80.4521 StartY=42.7351 StartZ=0 EndX=-80.4521 EndY=87.0314 EndZ=0
  constraints (8):
    c: Coincident(g0,g1)
    c: Coincident(g1,g2)
    c: Coincident(g2,g3)
    c: Coincident(g3,g0)
    c: Horizontal(g0)
    c: Horizontal(g2)
    c: Vertical(g1)
    c: Vertical(g3)
FEATURE [PartDesign::Body] Body002  label="faceAvant"
  BaseFeature = -> Slice_child1
  Group = -> [Clone001,Thickness001,DatumPlane007,Sketch016,Pad005,Sketch017,Pad006,Sketch018,Pocket010,DatumPlane011,Sketch030,Pad014,Pad015,Sketch031,Pad016,Sketch039,Pocket018,DatumPlane016,Sketch044]
  Origin = -> Origin003
  Tip = -> Pocket018
COMPONENT P2 — geometry summary ("theBoard"; no construction recipe available for this part):
  bounding box: 59.2 x 55.2 x 51.3 mm
  tessellated surface: 96,346 triangles
  volume: 9777 mm^3 (6% of its bounding box)
COMPONENT P3 — geometry summary ("dcdc_002"; no construction recipe available for this part):
  bounding box: 54.0 x 24.0 x 14.8 mm
  tessellated surface: 266,733 triangles
  volume: 4112 mm^3 (21% of its bounding box)
COMPONENT P4 — geometry summary ("usbFem001"; no construction recipe available for this part):
  bounding box: 22.8 x 17.0 x 15.8 mm
  tessellated surface: 90,788 triangles
  volume: 995 mm^3 (16% of its bounding box)
  symmetry: mirror-symmetric across its x mid-plane
COMPONENT P5 — geometry summary ("switch_002"; no construction recipe available for this part):
  bounding box: 19.2 x 16.9 x 10.5 mm
  tessellated surface: 316 triangles
  volume: 1179 mm^3 (35% of its bounding box)
  symmetry: mirror-symmetric across its x mid-plane
COMPONENT P6 — recipe-attached ("tigeLaiton001", modeled in this document).
Construction recipe (the document's own serialized feature program — sketch geometry with constraints, then the solid features built on it; lengths are millimeters unless a unit is written):

FEATURE [PartDesign::Plane] DatumPlane012  label="planBaseTige"
  AttachmentOffset = pos=(0,0,-5.18) rot=(0,0,1;0rad)
  Length = 60
  MapMode = 5
  Placement = pos=(-5.18,1.2e-15,-1.2e-15) rot=(0.57735,0.57735,0.57735;2.0944rad)
  ResizeMode = 0
  Support = -> [YZ_Plane012]
  Width = 60
  expr: .AttachmentOffset.Base.z = -<<tige>>.planBaseTigeposX
FEATURE [Sketcher::SketchObject] Sketch032  label="sk_tiges"
  FullyConstrained = true
  MapMode = 5
  Placement = pos=(-5.18,1.2e-15,-1.2e-15) rot=(0.57735,0.57735,0.57735;2.0944rad)
  Support = -> [DatumPlane012]
  expr: Constraints[0] = <<tige>>.tigeDiam
  expr: Constraints[1] = <<tige>>.tigePosY
  expr: Constraints[2] = <<tige>>.tigePosX
  sketch-geometry (1):
    g0: Circle CenterX=-14 CenterY=14.3 CenterZ=0 NormalX=0 NormalY=0 NormalZ=1 AngleXU=0 Radius=1.25
  constraints (3):
    c: Diameter(g0) = 2.5
    c: DistanceY(g-1,g0) = 14.3
    c: DistanceX(g0,g-1) = 14
FEATURE [PartDesign::Pad] Pad017  label="tigeBasse"
  AllowMultiFace = false
  Direction = (1,-1e-16,1e-16)
  Length = 33.62
  Length2 = 100
  Placement = pos=(-5.18,1.2e-15,-1.2e-15) rot=(0.57735,0.57735,0.57735;2.0944rad)
  Profile = -> Sketch032
  Reversed = true
  Type = 0
  expr: Length = <<tige>>.tigeLong
FEATURE [PartDesign::Body] Body007  label="tigeLaiton"
  Group = -> [DatumPlane012,Sketch032,Pad017]
  Origin = -> Origin016
  Tip = -> Pad017
FEATURE [PartDesign::Plane] DatumPlane013  label="planTige2"
  AttachmentOffset = pos=(0,0,-5.18) rot=(0,0,1;0rad)
  Length = 60
  MapMode = 5
  Placement = pos=(-5.18,1.2e-15,-1.2e-15) rot=(0.57735,0.57735,0.57735;2.0944rad)
  ResizeMode = 0
  Support = -> [YZ_Plane014]
  Width = 60
  expr: .AttachmentOffset.Base.z = -<<tige>>.planBaseTigeposX
FEATURE [Sketcher::SketchObject] Sketch033  label="sk_tige2"
  FullyConstrained = true
  MapMode = 5
  Placement = pos=(-5.18,1.2e-15,-1.2e-15) rot=(0.57735,0.57735,0.57735;2.0944rad)
  Support = -> [DatumPlane013]
  expr: Constraints[0] = <<tige>>.tigeDiam
  expr: Constraints[1] = <<tige>>.tigePosX
  expr: Constraints[2] = <<tige>>.tigePosY + <<tige>>.xtEcartBroches
  sketch-geometry (1):
    g0: Circle CenterX=-14 CenterY=21.86 CenterZ=0 NormalX=0 NormalY=0 NormalZ=1 AngleXU=0 Radius=1.25
  constraints (3):
    c: Diameter(g0) = 2.5
    c: DistanceX(g0,g-1) = 14
    c: DistanceY(g-1,g0) = 21.86
FEATURE [PartDesign::Pad] Pad018
  AllowMultiFace = false
  Direction = (1,-1e-16,1e-16)
  Length = 33.62
  Length2 = 100
  Placement = pos=(-5.18,1.2e-15,-1.2e-15) rot=(0.57735,0.57735,0.57735;2.0944rad)
  Profile = -> Sketch033
  Reversed = true
  Type = 0
  expr: Length = <<tige>>.tigeLong
FEATURE [PartDesign::Body] Body008  label="tige2"
  Group = -> [DatumPlane013,Sketch033,Pad018]
  Origin = -> Origin018
  Tip = -> Pad018
COMPONENT P7 — geometry summary ("xtVisInsertFix"; no construction recipe available for this part):
  bounding box: 20.2 x 17.7 x 16.6 mm
  tessellated surface: 21,960 triangles
  volume: 1306 mm^3 (22% of its bounding box)
COMPONENT P8 — geometry summary ("xtVisInertMob"; no construction recipe available for this part):
  bounding box: 20.5 x 17.8 x 16.5 mm
  tessellated surface: 31,880 triangles
  volume: 1060 mm^3 (18% of its bounding box)
COMPONENT P9 — recipe-attached ("visInsertFavFix", modeled in this document).
Construction recipe (the document's own serialized feature program — sketch geometry with constraints, then the solid features built on it; lengths are millimeters unless a unit is written):

FEATURE [Sketcher::SketchObject] Sketch034  label="Sketch"
  FullyConstrained = false
  MapMode = 5
  Support = -> [XY_Plane015]
  sketch-geometry (1):
    g0: Circle CenterX=0 CenterY=0 CenterZ=0 NormalX=0 NormalY=0 NormalZ=1 AngleXU=0 Radius=2.75
  constraints (2):
    c: Coincident(g0,g-1)
    c: Diameter(g0) = 5.5
FEATURE [PartDesign::Pad] Pad019  label="tete"
  AllowMultiFace = false
  Direction = (1,1,1)
  Length = 3
  Length2 = 100
  Profile = -> Sketch034
  Type = 0
FEATURE [Sketcher::SketchObject] Sketch001
  FullyConstrained = false
  MapMode = 5
  Placement = pos=(0,0,0) rot=(1,0,0;3.14159rad)
  Support = -> [Pad019]
  sketch-geometry (1):
    g0: Circle CenterX=0 CenterY=0 CenterZ=0 NormalX=0 NormalY=0 NormalZ=1 AngleXU=0 Radius=1.5
  constraints (2):
    c: Coincident(g0,g-1)
    c: Diameter(g0) = 3
FEATURE [PartDesign::Pad] Pad020  label="corps"
  AllowMultiFace = false
  BaseFeature = -> Pad019
  Direction = (1,1,1)
  Length = 6
  Length2 = 100
  Profile = -> Sketch001
  Type = 0
FEATURE [PartDesign::Plane] DatumPlane014
  AttachmentOffset = pos=(0,0,3) rot=(0,0,1;0rad)
  Length = 60
  MapMode = 5
  Placement = pos=(0,0,3) rot=(0,0,1;0rad)
  ResizeMode = 0
  Support = -> [XY_Plane015]
  Width = 60
FEATURE [Sketcher::SketchObject] Sketch035  label="Sketch002"
  FullyConstrained = false
  MapMode = 5
  Placement = pos=(0,0,3) rot=(0,0,1;0rad)
  Support = -> [DatumPlane014]
  sketch-geometry (7):
    g0: LineSegment StartX=0.721688 StartY=-1.25 StartZ=0 EndX=1.44338 EndY=1.0119e-12 EndZ=0
    g1: LineSegment StartX=1.44338 StartY=1.0119e-12 StartZ=0 EndX=0.721688 EndY=1.25 EndZ=0
    g2: LineSegment StartX=0.721688 StartY=1.25 StartZ=0 EndX=-0.721688 EndY=1.25 EndZ=0
    g3: LineSegment StartX=-0.721688 StartY=1.25 StartZ=0 EndX=-1.44338 EndY=8.689e-13 EndZ=0
    g4: LineSegment StartX=-1.44338 StartY=8.689e-13 StartZ=0 EndX=-0.721688 EndY=-1.25 EndZ=0
    g5: LineSegment StartX=-0.721688 StartY=-1.25 StartZ=0 EndX=0.721688 EndY=-1.25 EndZ=0
    g6: Circle CenterX=0 CenterY=0 CenterZ=0 NormalX=0 NormalY=0 NormalZ=1 AngleXU=0 Radius=1.44338
  constraints (16):
    c: Coincident(g0,g1)
    c: Coincident(g1,g2)
    c: Coincident(g2,g3)
    c: Coincident(g3,g4)
    c: Coincident(g4,g5)
    c: Coincident(g5,g0)
    c: Equal(g0, g1-g5) x5
    c: PointOnObject(g0,g6)
    c: PointOnObject(g1,g6)
    c: PointOnObject(g2,g6)
    c: PointOnObject(g3,g6)
    c: PointOnObject(g4,g6)
    c: PointOnObject(g5,g6)
    c: Coincident(g6,g-1)
    c: Horizontal(g2)
    c: DistanceY(g0,g1) = 2.5
FEATURE [PartDesign::Pocket] Pocket016  label="emprunte"
  AllowMultiFace = false
  BaseFeature = -> Pad020
  Direction = (1,1,1)
  Length = 4
  Length2 = 100
  Profile = -> Sketch035
  Type = 0
FEATURE [PartDesign::Body] Body009  label="visTHCM3x6_FAV001"
  Group = -> [Sketch034,Pad019,Sketch001,Pad020,DatumPlane014,Sketch035,Pocket016]
  Origin = -> Origin019
  Placement = pos=(-6.5,-61.8718,6.01041) rot=(1,0,0;3.92699rad)
  Tip = -> Pocket016
COMPONENT P10 — recipe-attached ("visInserFavMob", modeled in this document).
Construction recipe (the document's own serialized feature program — sketch geometry with constraints, then the solid features built on it; lengths are millimeters unless a unit is written):

FEATURE [Sketcher::SketchObject] Sketch036
  FullyConstrained = false
  MapMode = 5
  Support = -> [XY_Plane016]
  sketch-geometry (1):
    g0: Circle CenterX=0 CenterY=0 CenterZ=0 NormalX=0 NormalY=0 NormalZ=1 AngleXU=0 Radius=2.75
  constraints (2):
    c: Coincident(g0,g-1)
    c: Diameter(g0) = 5.5
FEATURE [PartDesign::Pad] Pad021  label="tete001"
  AllowMultiFace = false
  Direction = (1,1,1)
  Length = 3
  Length2 = 100
  Profile = -> Sketch036
  Type = 0
FEATURE [Sketcher::SketchObject] Sketch037
  FullyConstrained = false
  MapMode = 5
  Placement = pos=(0,0,0) rot=(1,0,0;3.14159rad)
  Support = -> [Pad021]
  sketch-geometry (1):
    g0: Circle CenterX=0 CenterY=0 CenterZ=0 NormalX=0 NormalY=0 NormalZ=1 AngleXU=0 Radius=1.5
  constraints (2):
    c: Coincident(g0,g-1)
    c: Diameter(g0) = 3
FEATURE [PartDesign::Pad] Pad022  label="corps001"
  AllowMultiFace = false
  BaseFeature = -> Pad021
  Direction = (1,1,1)
  Length = 6
  Length2 = 100
  Profile = -> Sketch037
  Type = 0
FEATURE [PartDesign::Plane] DatumPlane015
  AttachmentOffset = pos=(0,0,3) rot=(0,0,1;0rad)
  Length = 60
  MapMode = 5
  Placement = pos=(0,0,3) rot=(0,0,1;0rad)
  ResizeMode = 0
  Support = -> [XY_Plane016]
  Width = 60
FEATURE [Sketcher::SketchObject] Sketch038
  FullyConstrained = false
  MapMode = 5
  Placement = pos=(0,0,3) rot=(0,0,1;0rad)
  Support = -> [DatumPlane015]
  sketch-geometry (7):
    g0: LineSegment StartX=0.721688 StartY=-1.25 StartZ=0 EndX=1.44338 EndY=1.0119e-12 EndZ=0
    g1: LineSegment StartX=1.44338 StartY=1.0119e-12 StartZ=0 EndX=0.721688 EndY=1.25 EndZ=0
    g2: LineSegment StartX=0.721688 StartY=1.25 StartZ=0 EndX=-0.721688 EndY=1.25 EndZ=0
    g3: LineSegment StartX=-0.721688 StartY=1.25 StartZ=0 EndX=-1.44338 EndY=8.689e-13 EndZ=0
    g4: LineSegment StartX=-1.44338 StartY=8.689e-13 StartZ=0 EndX=-0.721688 EndY=-1.25 EndZ=0
    g5: LineSegment StartX=-0.721688 StartY=-1.25 StartZ=0 EndX=0.721688 EndY=-1.25 EndZ=0
    g6: Circle CenterX=0 CenterY=0 CenterZ=0 NormalX=0 NormalY=0 NormalZ=1 AngleXU=0 Radius=1.44338
  constraints (16):
    c: Coincident(g0,g1)
    c: Coincident(g1,g2)
    c: Coincident(g2,g3)
    c: Coincident(g3,g4)
    c: Coincident(g4,g5)
    c: Coincident(g5,g0)
    c: Equal(g0, g1-g5) x5
    c: PointOnObject(g0,g6)
    c: PointOnObject(g1,g6)
    c: PointOnObject(g2,g6)
    c: PointOnObject(g3,g6)
    c: PointOnObject(g4,g6)
    c: PointOnObject(g5,g6)
    c: Coincident(g6,g-1)
    c: Horizontal(g2)
    c: DistanceY(g0,g1) = 2.5
FEATURE [PartDesign::Pocket] Pocket017  label="emprunte001"
  AllowMultiFace = false
  BaseFeature = -> Pad022
  Direction = (1,1,1)
  Length = 4
  Length2 = 100
  Profile = -> Sketch038
  Type = 0
FEATURE [PartDesign::Body] Body010  label="visTHCM3x6_FAV002"
  Group = -> [Sketch036,Pad021,Sketch037,Pad022,DatumPlane015,Sketch038,Pocket017]
  Origin = -> Origin020
  Placement = pos=(-43.5,-61.8718,6.01041) rot=(1,0,0;3.92699rad)
  Tip = -> Pocket017
  expr: .Placement.Base.x = -(<<sp>>.largeurModuleBase - 6.5)
COMPONENT P11 — geometry summary ("poubelle"; no construction recipe available for this part):
  bounding box: 43.6 x 34.0 x 34.0 mm
  tessellated surface: 3,984 triangles
  volume: 4442 mm^3 (9% of its bounding box)
PROVENANCE & LICENSES
A FreeCAD (.FCStd) document from a public repository crawl; recipes are the document's own serialized feature recipes (and, for linked parts, companion documents' recipes).
License: as declared in the source repository (recorded in the dataset sidecar).
